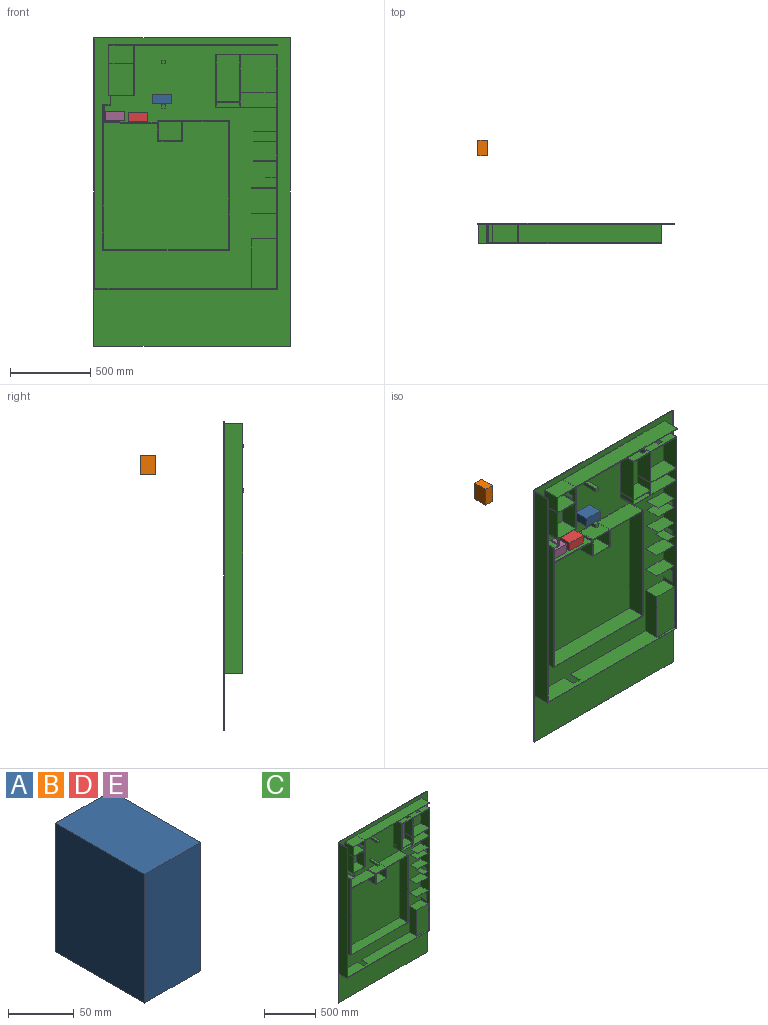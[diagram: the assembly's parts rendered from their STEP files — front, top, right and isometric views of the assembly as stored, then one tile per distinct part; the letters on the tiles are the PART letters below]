
ASSEMBLY  parts=5 mates=3
PART A: 6 faces, bbox 60x96x120 mm
  f0: plane 120x96mm, normal (1,0,0), area 11520mm2, adj f1,f3,f4,f5
  f1: plane 96x60mm, normal (0,0,1), area 5760mm2, adj f0,f2,f4,f5
  f2: plane 120x96mm, normal (-1,0,0), area 11520mm2, adj f1,f3,f4,f5
  f3: plane 96x60mm, normal (0,0,-1), area 5760mm2, adj f0,f2,f4,f5
  f4: plane 120x60mm, normal (0,-1,0), area 7200mm2, adj f0,f1,f2,f3
  f5: plane 120x60mm, normal (0,1,0), area 7200mm2, adj f0,f1,f2,f3
PART B: same geometry as A
PART C: 146 faces, bbox 1219.9x125x1915.2 mm
  f0: plane 1122x115mm, normal (-1,0,0), area 85376.8mm2, adj f1,f2,f8,f54,f97,f98,f99,f100
  f1: plane 1127x115mm, normal (0,0,1), area 108788.9mm2, adj f0,f2,f54,f108,f109,f110,f111,f112
  f2: plane 1915.2x1219.86mm, normal (0,-1,0), area 2188020.2mm2, adj f0,f1,f3,f4,f5,f6,f7,f8
  f3: plane 777x115mm, normal (0,0,1), area 89355mm2, adj f2,f5,f48,f114
  f4: plane 1137x115mm, normal (0,0,-1), area 119738.9mm2, adj f2,f6,f54,f106,f108,f109,f110,f111
  f5: plane 794x115mm, normal (-1,0,0), area 91310mm2, adj f2,f3,f39,f48
  f6: plane 1461x115mm, normal (1,0,0), area 155615mm2, adj f2,f4,f12,f54,f97,f98,f99,f100
  f7: plane 1219.86x5mm, normal (0,0,-1), area 6099.3mm2, adj f2,f23,f25,f26
  f8: plane 377x115mm, normal (0,0,-1), area 43355mm2, adj f0,f2,f52,f54
  f9: plane 144x115mm, normal (0,0,-1), area 16560mm2, adj f10,f48,f94,f96
  f10: plane 144x120mm, normal (0,-1,0), area 17280mm2, adj f9,f94,f95,f96
  f11: plane 144x115mm, normal (0,0,-1), area 13284mm2, adj f2,f53,f54,f62,f75,f76,f77
  f12: plane 382x115mm, normal (0,0,1), area 37378mm2, adj f2,f6,f52,f54,f75,f76,f77,f78
  f13: plane 115x57mm, normal (1,0,0), area 2470.1mm2, adj f2,f29,f46,f48,f72,f73,f74
  f14: plane 115x52mm, normal (-1,0,0), area 1895.1mm2, adj f2,f35,f36,f48,f72,f73,f74
  f15: plane 115x111mm, normal (-1,0,0), area 9489mm2, adj f2,f47,f48,f65,f66,f67,f68
  f16: plane 315x115mm, normal (1,0,0), area 29673mm2, adj f2,f29,f30,f48,f66,f67,f68,f69
  f17: plane 194x115mm, normal (-1,0,0), area 19034mm2, adj f2,f27,f48,f64,f69,f70,f71
  f18: plane 115x111mm, normal (1,0,0), area 12765mm2, adj f2,f47,f48,f65
  f19: plane 144x31mm, normal (0,-1,0), area 4464mm2, adj f22,f51,f56,f57
  f20: plane 231x115mm, normal (-1,0,0), area 26565mm2, adj f2,f49,f54,f60
  f21: plane 223x115mm, normal (0,0,1), area 25645mm2, adj f50,f54,f55,f58
  f22: plane 115x31mm, normal (1,0,0), area 3565mm2, adj f19,f51,f54,f56
  f23: plane 1915.2x5mm, normal (1,0,0), area 9576mm2, adj f2,f7,f24,f26
  f24: plane 1219.86x5mm, normal (0,0,1), area 6099.3mm2, adj f2,f23,f25,f26
  f25: plane 1915.2x5mm, normal (-1,0,0), area 9576mm2, adj f2,f7,f24,f26
  f26: plane 1915.2x1219.86mm, normal (0,1,0), area 2336281.1mm2, adj f7,f23,f24,f25
  f27: plane 155x115mm, normal (0,0,1), area 17825mm2, adj f2,f17,f28,f48
  f28: plane 194x115mm, normal (1,0,0), area 22310mm2, adj f2,f27,f48,f64
  f29: plane 147x115mm, normal (0,0,-1), area 16905mm2, adj f2,f13,f16,f48
  f30: plane 889x115mm, normal (0,0,-1), area 102235mm2, adj f2,f16,f31,f48
  f31: plane 115x5mm, normal (1,0,0), area 575mm2, adj f2,f30,f32,f48
  f32: plane 1054x115mm, normal (0,0,1), area 121210mm2, adj f2,f31,f33,f48
  f33: plane 319.83x115mm, normal (-1,0,0), area 36780.8mm2, adj f2,f32,f34,f48
  f34: plane 115x5mm, normal (-0.03,0,-1), area 575.3mm2, adj f2,f33,f35,f48
  f35: plane 115x8mm, normal (0,0,-1), area 920mm2, adj f2,f14,f34,f48
  f36: plane 115x40mm, normal (0,0,1), area 4600mm2, adj f2,f14,f37,f48
  f37: plane 115x114.21mm, normal (-1,0,0), area 13133.8mm2, adj f2,f36,f38,f48
  f38: plane 336.94x115mm, normal (-0.02,0,-1), area 38754.8mm2, adj f2,f37,f48,f91
  f39: plane 285x115mm, normal (0,0,-1), area 32775mm2, adj f2,f5,f48,f93
  f40: plane 787x115mm, normal (0,0,-1), area 90505mm2, adj f2,f41,f48,f107
  f41: plane 804x115mm, normal (1,0,0), area 92460mm2, adj f2,f40,f42,f48
  f42: plane 449x115mm, normal (0,0,1), area 51635mm2, adj f2,f41,f43,f48
  f43: plane 115x12mm, normal (-1,0,0), area 1380mm2, adj f2,f42,f44,f48
  f44: plane 326.94x115mm, normal (0.02,0,1), area 37605mm2, adj f2,f43,f45,f48
  f45: plane 115x103mm, normal (1,0,0), area 11845mm2, adj f2,f44,f46,f48
  f46: plane 115x40mm, normal (0,0,-1), area 4600mm2, adj f2,f13,f45,f48
  f47: plane 155x115mm, normal (0,0,-1), area 17825mm2, adj f2,f15,f18,f48
  f48: plane 1278.1x1087.06mm, normal (0,-1,0), area 29718.5mm2, adj f3,f5,f9,f13,f14,f15,f16,f17
  f49: plane 223x115mm, normal (0,0,-1), area 22369mm2, adj f2,f20,f54,f61,f78,f79,f80
  f50: plane 115x88mm, normal (-1,0,0), area 10120mm2, adj f21,f54,f55,f59
  f51: plane 144x115mm, normal (0,0,1), area 16560mm2, adj f19,f22,f54,f57
  f52: plane 334x115mm, normal (-1,0,0), area 38410mm2, adj f2,f8,f12,f54
  f53: plane 288x115mm, normal (1,0,0), area 33120mm2, adj f2,f11,f54,f63
  f54: plane 1550x1137mm, normal (0,-1,0), area 29535mm2, adj f0,f1,f4,f6,f8,f11,f12,f20
  f55: plane 223x88mm, normal (0,-1,0), area 19624mm2, adj f21,f50,f58,f59
  f56: plane 144x115mm, normal (0,0,-1), area 16560mm2, adj f19,f22,f54,f57
  f57: plane 115x31mm, normal (-1,0,0), area 3565mm2, adj f19,f51,f54,f56
  f58: plane 115x88mm, normal (1,0,0), area 10120mm2, adj f21,f54,f55,f59
  f59: plane 223x115mm, normal (0,0,-1), area 25645mm2, adj f50,f54,f55,f58
  f60: plane 223x115mm, normal (0,0,1), area 25645mm2, adj f2,f20,f54,f61
  f61: plane 231x115mm, normal (1,0,0), area 26565mm2, adj f2,f49,f54,f60
  f62: plane 288x115mm, normal (-1,0,0), area 33120mm2, adj f2,f11,f54,f63
  f63: plane 144x115mm, normal (0,0,1), area 16560mm2, adj f2,f53,f54,f62
  f64: plane 155x115mm, normal (0,0,-1), area 17825mm2, adj f2,f17,f28,f48
  f65: plane 155x115mm, normal (0,0,1), area 17825mm2, adj f2,f15,f18,f48
  f66: plane 91x5mm, normal (0,0,1), area 455mm2, adj f2,f15,f16,f68
  f67: plane 91x5mm, normal (0,0,-1), area 455mm2, adj f2,f15,f16,f68
  f68: plane 36x5mm, normal (0,1,0), area 180mm2, adj f15,f16,f66,f67
  f69: plane 91x5mm, normal (0,0,-1), area 455mm2, adj f2,f16,f17,f70
  f70: plane 36x5mm, normal (0,1,0), area 180mm2, adj f16,f17,f69,f71
  f71: plane 91x5mm, normal (0,0,1), area 455mm2, adj f2,f16,f17,f70
  f72: plane 39.29x5mm, normal (0,1,0), area 196.4mm2, adj f13,f14,f73,f74
  f73: plane 103.98x5mm, normal (0,0,1), area 519.9mm2, adj f2,f13,f14,f72
  f74: plane 103.98x5mm, normal (0,0,-1), area 519.9mm2, adj f2,f13,f14,f72
  f75: plane 91x5mm, normal (-1,0,0), area 455mm2, adj f2,f11,f12,f77
  f76: plane 91x5mm, normal (1,0,0), area 455mm2, adj f2,f11,f12,f77
  f77: plane 36x5mm, normal (0,1,0), area 180mm2, adj f11,f12,f75,f76
  f78: plane 91x5mm, normal (1,0,0), area 455mm2, adj f2,f12,f49,f80
  f79: plane 91x5mm, normal (-1,0,0), area 455mm2, adj f2,f12,f49,f80
  f80: plane 36x5mm, normal (0,1,0), area 180mm2, adj f12,f49,f78,f79
  f81: plane 120x24mm, normal (1,0,0), area 2880mm2, adj f2,f82,f84,f85
  f82: plane 120x24mm, normal (0,0,1), area 2880mm2, adj f2,f81,f83,f85
  f83: plane 120x24mm, normal (-1,0,0), area 2880mm2, adj f2,f82,f84,f85
  f84: plane 120x24mm, normal (0,0,-1), area 2880mm2, adj f2,f81,f83,f85
  f85: plane 24x24mm, normal (0,-1,0), area 576mm2, adj f81,f82,f83,f84
  f86: plane 120x24mm, normal (1,0,0), area 2880mm2, adj f2,f87,f89,f90
  f87: plane 120x24mm, normal (0,0,1), area 2880mm2, adj f2,f86,f88,f90
  f88: plane 120x24mm, normal (-1,0,0), area 2880mm2, adj f2,f87,f89,f90
  f89: plane 120x24mm, normal (0,0,-1), area 2880mm2, adj f2,f86,f88,f90
  f90: plane 24x24mm, normal (0,-1,0), area 576mm2, adj f86,f87,f88,f89
  f91: plane 115x111.81mm, normal (-1,0,0), area 12857.9mm2, adj f2,f38,f48,f92
  f92: plane 154x115mm, normal (0,0,-1), area 17710mm2, adj f2,f48,f91,f93
  f93: plane 125x115mm, normal (1,0,0), area 14375mm2, adj f2,f39,f48,f92
  f94: plane 120x115mm, normal (-1,0,0), area 13800mm2, adj f9,f10,f48,f95
  f95: plane 144x115mm, normal (0,0,1), area 16560mm2, adj f10,f48,f94,f96
  f96: plane 120x115mm, normal (1,0,0), area 13800mm2, adj f9,f10,f48,f95
  f97: plane 80x5mm, normal (0,0,-1), area 400mm2, adj f0,f2,f6,f99
  f98: plane 80x5mm, normal (0,0,1), area 400mm2, adj f0,f2,f6,f99
  f99: plane 87x5mm, normal (0,1,0), area 435mm2, adj f0,f6,f97,f98
  f100: plane 80x5mm, normal (0,0,-1), area 400mm2, adj f0,f2,f6,f102
  f101: plane 100x71mm, normal (0,0,1), area 7000mm2, adj f0,f2,f6,f102,f131,f133
  f102: plane 34x5mm, normal (0,1,0), area 170mm2, adj f0,f6,f100,f101
  f103: plane 80x5mm, normal (0,0,-1), area 400mm2, adj f0,f2,f6,f105
  f104: plane 80x5mm, normal (0,0,1), area 400mm2, adj f0,f2,f6,f105
  f105: plane 34x5mm, normal (0,1,0), area 170mm2, adj f0,f6,f103,f104,f122
  f106: plane 1550x115mm, normal (-1,0,0), area 178250mm2, adj f2,f4,f54,f117
  f107: plane 906x115mm, normal (-1,0,0), area 104190mm2, adj f2,f40,f48,f115
  f108: plane 87.11x5mm, normal (-1,0,0), area 435.6mm2, adj f1,f2,f4,f110
  f109: plane 87.11x5mm, normal (1,0,0), area 435.6mm2, adj f1,f2,f4,f110
  f110: plane 57x5mm, normal (0,1,0), area 285mm2, adj f1,f4,f108,f109
  f111: plane 104.32x5mm, normal (-1,0,0), area 521.6mm2, adj f1,f2,f4,f113,f142
  f112: plane 104.32x5mm, normal (1,0,0), area 521.6mm2, adj f1,f2,f4,f113,f142
  f113: plane 58x5mm, normal (0,1,0), area 290mm2, adj f1,f4,f111,f112
  f114: plane 901x115mm, normal (1,0,0), area 103615mm2, adj f2,f3,f48,f115
  f115: plane 115x5mm, normal (0,0,1), area 575mm2, adj f2,f48,f107,f114
  f116: plane 1545x115mm, normal (1,0,0), area 177675mm2, adj f1,f2,f54,f117
  f117: plane 115x5mm, normal (0,0,1), area 575mm2, adj f2,f54,f106,f116
  f118: plane 144x100mm, normal (0,0,1), area 14400mm2, adj f0,f2,f119,f121
  f119: plane 100x1mm, normal (-1,0,0), area 100mm2, adj f2,f118,f120,f121
  f120: plane 144x100mm, normal (0,0,-1), area 14400mm2, adj f0,f2,f119,f121
  f121: plane 144x1mm, normal (0,-1,0), area 144mm2, adj f0,f118,f119,f120
  f122: plane 80x1mm, normal (1,0,0), area 80mm2, adj f2,f105,f123,f125
  f123: plane 144x100mm, normal (0,0,1), area 14400mm2, adj f0,f2,f122,f124,f126
  f124: plane 100x1mm, normal (-1,0,0), area 100mm2, adj f2,f123,f125,f126
  f125: plane 144x100mm, normal (0,0,-1), area 14400mm2, adj f0,f2,f122,f124,f126
  f126: plane 144x1mm, normal (0,-1,0), area 144mm2, adj f0,f123,f124,f125
  f127: plane 144x100mm, normal (0,0,1), area 14400mm2, adj f0,f2,f128,f130
  f128: plane 100x1mm, normal (-1,0,0), area 100mm2, adj f2,f127,f129,f130
  f129: plane 144x100mm, normal (0,0,-1), area 14400mm2, adj f0,f2,f128,f130
  f130: plane 144x1mm, normal (0,-1,0), area 144mm2, adj f0,f127,f128,f129
  f131: plane 100x1mm, normal (-1,0,0), area 100mm2, adj f2,f101,f132,f133
  f132: plane 100x66mm, normal (0,0,-1), area 6600mm2, adj f0,f2,f131,f133
  f133: plane 66x1mm, normal (0,-1,0), area 66mm2, adj f0,f101,f131,f132
  f134: plane 156x100mm, normal (0,0,1), area 15600mm2, adj f0,f2,f135,f137
  f135: plane 100x1mm, normal (-1,0,0), area 100mm2, adj f2,f134,f136,f137
  f136: plane 156x100mm, normal (0,0,-1), area 15600mm2, adj f0,f2,f135,f137
  f137: plane 156x1mm, normal (0,-1,0), area 156mm2, adj f0,f134,f135,f136
  f138: plane 156x100mm, normal (0,0,-1), area 15600mm2, adj f0,f2,f140,f141
  f139: plane 156x100mm, normal (0,0,1), area 15600mm2, adj f0,f2,f140,f141
  f140: plane 100x1mm, normal (-1,0,0), area 100mm2, adj f2,f138,f139,f141
  f141: plane 156x1mm, normal (0,-1,0), area 156mm2, adj f0,f138,f139,f140
  f142: plane 100x58mm, normal (0,0,-1), area 5800mm2, adj f2,f111,f112,f145
  f143: plane 156x100mm, normal (0,0,1), area 15600mm2, adj f0,f2,f144,f145
  f144: plane 307.33x100mm, normal (-1,0,0), area 30733.2mm2, adj f1,f2,f143,f145
  f145: plane 307.33x156mm, normal (0,-1,0), area 47943.8mm2, adj f0,f1,f142,f143,f144
PART D: same geometry as A
PART E: same geometry as A
PLACE A rot(axis=(-0.71,0,0.71),180deg) t=(79.09,-308.4,-66.94)mm
PLACE B rot(axis=(1,0,0),180deg) t=(-316.34,214.08,47.51)mm
PLACE C t=(135.19,-207.4,347.96)mm fixed
PLACE D rot(axis=(-0.71,0,0.71),180deg) t=(-69.94,-308.4,-177.41)mm
PLACE E rot(axis=(-0.71,0,-0.71),180deg) t=(-214.38,-308.4,-171.39)mm
MATE planar A.f4 <-> C.f2  axis (0,1,0) through (79.09,-212.4,-66.94)mm
MATE planar D.f4 <-> C.f2  axis (0,1,0) through (-69.94,-212.4,-177.41)mm
MATE planar E.f4 <-> C.f2  axis (0,1,0) through (-214.38,-212.4,-171.39)mm
